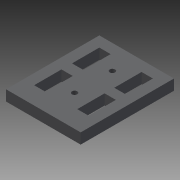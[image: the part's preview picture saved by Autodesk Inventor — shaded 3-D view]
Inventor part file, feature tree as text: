
AUTODESK INVENTOR PART (.ipt)
format: ipt  version: 2013 (Build 170138000, 138)  size: 102,400 bytes
history: native  units: mm
features: extrude x1, sketch x1
ambient origin geometry x8: Origin, YZ Plane, XZ Plane, XY Plane, X Axis, Y Axis, Z Axis, Center Point
bodies: Solid1 (feature_tree)
feature tree (2):
  extrude  "Extrusion1"  [1 undecoded]
  sketch  "Sketch1"  dims[d0=6.0mm d1=0.0mm]
note: 1 required parameter value undecoded (feature->parameter linkage not recoverable at this tier; creation-order binding heuristic only, values carry confidence <= 0.55)
